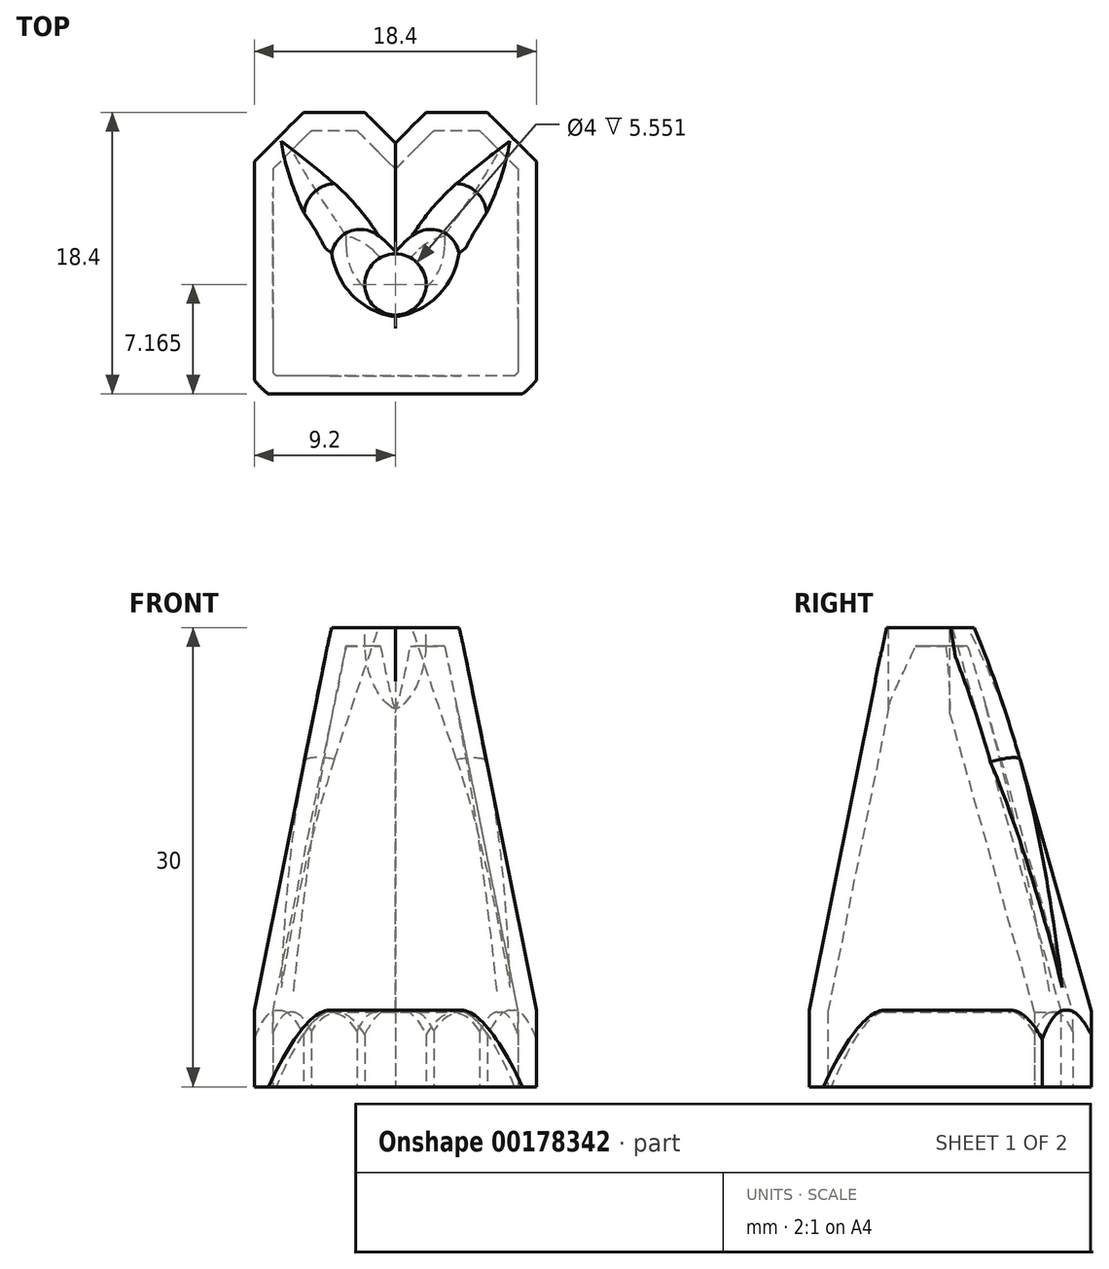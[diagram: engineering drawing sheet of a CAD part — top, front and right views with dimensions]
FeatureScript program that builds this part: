
annotation { "Feature Type Name" : "Feature", "Feature Type Description" : "" }
export const myFeature = defineFeature(function(context is Context, id is Id, definition is map)
    precondition{}
    {
        {
            var Q0;
            Q0=qCreatedBy(makeId("Top.planeOp"),FACE);
            var sketch = newSketch(context, id + "F0", { "sketchPlane" : qUnion([Q0])});
            skLineSegment(sketch, "E0.bottom", {"start": v(5.5, 8) * mm, "end": v(2.5, 8) * mm});
            skLineSegment(sketch, "E0.top", {"start": v(8, -8) * mm, "end": v(-8, -8) * mm});
            skLineSegment(sketch, "E0.left", {"start": v(8, 5.5) * mm, "end": v(8, -8) * mm});
            skLineSegment(sketch, "E0.right", {"start": v(-8, 5.5) * mm, "end": v(-8, -8) * mm});
            skPoint(sketch, "E0.middle", {"position": v(0, 0) * mm});
            skLineSegment(sketch, "E1", {"start": v(-2.5, 8) * mm, "end": v(0, 5.5) * mm});
            skLineSegment(sketch, "E2", {"start": v(0, 5.5) * mm, "end": v(2.5, 8) * mm});
            skLineSegment(sketch, "E3", {"start": v(-8, 5.5) * mm, "end": v(-5.5, 8) * mm});
            skLineSegment(sketch, "E4", {"start": v(8, 5.5) * mm, "end": v(5.5, 8) * mm});
            skPoint(sketch, "E5.orphan", {"position": v(-8, 8) * mm});
            skLineSegment(sketch, "E6.trimOffspring", {"start": v(-2.5, 8) * mm, "end": v(-5.5, 8) * mm});
            skPoint(sketch, "E7.orphan", {"position": v(8, 8) * mm});
            skLineSegment(sketch, "E8.0", {"start": v(-2, 9.2) * mm, "end": v(-6, 9.2) * mm});
            skLineSegment(sketch, "E8.1", {"start": v(-9.2, 6) * mm, "end": v(-6, 9.2) * mm});
            skLineSegment(sketch, "E8.2", {"start": v(-2, 9.2) * mm, "end": v(0, 7.2) * mm});
            skLineSegment(sketch, "E8.3", {"start": v(-9.2, 6) * mm, "end": v(-9.2, -9.2) * mm});
            skLineSegment(sketch, "E8.4", {"start": v(9.2, -9.2) * mm, "end": v(-9.2, -9.2) * mm});
            skLineSegment(sketch, "E8.5", {"start": v(0, 7.2) * mm, "end": v(2, 9.2) * mm});
            skLineSegment(sketch, "E8.6", {"start": v(6, 9.2) * mm, "end": v(2, 9.2) * mm});
            skLineSegment(sketch, "E8.7", {"start": v(9.2, 6) * mm, "end": v(6, 9.2) * mm});
            skLineSegment(sketch, "E8.8", {"start": v(9.2, 6) * mm, "end": v(9.2, -9.2) * mm});
            skSolve(sketch);
        }
        {
            var Q0;
            Q0=makeQuery(id+"F0.imprint","IMPRINT",FACE,{"disambiguationData":[TD([[makeQuery(id+"F0.imprint","IMPRINT",EDGE,{"derivedFrom":sQuery(id+"F0.wireOp",EDGE,"E0.bottom")}),-1.0]])]});
            var Q1;
            Q1=makeQuery(id+"F0.imprint","IMPRINT",FACE,{"disambiguationData":[TD([[makeQuery(id+"F0.imprint","IMPRINT",EDGE,{"derivedFrom":sQuery(id+"F0.wireOp",EDGE,"E0.bottom")}),1.0]])]});
            extrude(context, id + "F1", {"entities" : qUnion([Q0, Q1]), "depth" : 30 * mm});
        }
        {
            var Q0;
            Q0=makeQuery(id+"F1.opExtrude","CAP_EDGE",EDGE,{"disambiguationData":[OSD([sQuery(id+"F0.wireOp",EDGE,"E8.3")])],"isStart":false});
            var Q1;
            Q1=makeQuery(id+"F1.opExtrude","CAP_FACE",FACE,{"disambiguationData":[OSD([sQuery(id+"F0.wireOp",EDGE,"E8.0"),sQuery(id+"F0.wireOp",EDGE,"E8.1"),sQuery(id+"F0.wireOp",EDGE,"E8.2"),sQuery(id+"F0.wireOp",EDGE,"E8.3"),sQuery(id+"F0.wireOp",EDGE,"E8.4"),sQuery(id+"F0.wireOp",EDGE,"E8.5"),sQuery(id+"F0.wireOp",EDGE,"E8.6"),sQuery(id+"F0.wireOp",EDGE,"E8.7"),sQuery(id+"F0.wireOp",EDGE,"E8.8")])],"isStart":false});
            chamfer(context, id + "F2", {"entities" : qUnion([Q0, Q1]), "chamferType" : ChamferType.TWO_OFFSETS, "width1" : 5 * mm, "oppositeDirection" : false, "width2" : 25 * mm, "tangentPropagation" : true});
        }
        {
            var Q0;
            Q0=makeQuery(id+"F2.opChamfer","BLEND_EDGE",EDGE,{"blendedFrom":[makeQuery(id+"F1.opExtrude","CAP_EDGE",EDGE,{"disambiguationData":[OSD([sQuery(id+"F0.wireOp",EDGE,"E8.1")])],"isStart":false}),makeQuery(id+"F1.opExtrude","CAP_EDGE",EDGE,{"disambiguationData":[OSD([sQuery(id+"F0.wireOp",EDGE,"E8.2")])],"isStart":false})],"blendedInto":[]});
            var Q1;
            Q1=makeQuery(id+"F2.opChamfer","BLEND_EDGE",EDGE,{"blendedFrom":[makeQuery(id+"F1.opExtrude","CAP_EDGE",EDGE,{"disambiguationData":[OSD([sQuery(id+"F0.wireOp",EDGE,"E8.5")])],"isStart":false}),makeQuery(id+"F1.opExtrude","CAP_EDGE",EDGE,{"disambiguationData":[OSD([sQuery(id+"F0.wireOp",EDGE,"E8.7")])],"isStart":false})],"blendedInto":[]});
            var Q2;
            Q2=makeQuery(id+"F2.opChamfer","BLEND_EDGE",EDGE,{"blendedFrom":[makeQuery(id+"F1.opExtrude","CAP_EDGE",EDGE,{"disambiguationData":[OSD([sQuery(id+"F0.wireOp",EDGE,"E8.1")])],"isStart":false}),makeQuery(id+"F1.opExtrude","CAP_EDGE",EDGE,{"disambiguationData":[OSD([sQuery(id+"F0.wireOp",EDGE,"E8.3")])],"isStart":false})],"blendedInto":[]});
            var Q3;
            Q3=makeQuery(id+"F2.opChamfer","BLEND_EDGE",EDGE,{"blendedFrom":[makeQuery(id+"F1.opExtrude","CAP_EDGE",EDGE,{"disambiguationData":[OSD([sQuery(id+"F0.wireOp",EDGE,"E8.7")])],"isStart":false}),makeQuery(id+"F1.opExtrude","CAP_EDGE",EDGE,{"disambiguationData":[OSD([sQuery(id+"F0.wireOp",EDGE,"E8.8")])],"isStart":false})],"blendedInto":[]});
            var Q4;
            Q4=makeQuery(id+"F2.opChamfer","BLEND_EDGE",EDGE,{"blendedFrom":[makeQuery(id+"F1.opExtrude","CAP_EDGE",EDGE,{"disambiguationData":[OSD([sQuery(id+"F0.wireOp",EDGE,"E8.3")])],"isStart":false}),makeQuery(id+"F1.opExtrude","CAP_EDGE",EDGE,{"disambiguationData":[OSD([sQuery(id+"F0.wireOp",EDGE,"E8.4")])],"isStart":false})],"blendedInto":[]});
            var Q5;
            Q5=makeQuery(id+"F2.opChamfer","BLEND_EDGE",EDGE,{"blendedFrom":[makeQuery(id+"F1.opExtrude","CAP_EDGE",EDGE,{"disambiguationData":[OSD([sQuery(id+"F0.wireOp",EDGE,"E8.4")])],"isStart":false}),makeQuery(id+"F1.opExtrude","CAP_EDGE",EDGE,{"disambiguationData":[OSD([sQuery(id+"F0.wireOp",EDGE,"E8.8")])],"isStart":false})],"blendedInto":[]});
            fillet(context, id + "F3", {"entities" : qUnion([Q0, Q1, Q2, Q3, Q4, Q5]), "radius" : 5 * mm, "tangentPropagation" : true, "allowEdgeOverflow" : false});
        }
        {
            var Q0;
            Q0=makeQuery(id+"F1.opExtrude","CAP_FACE",FACE,{"disambiguationData":[OSD([sQuery(id+"F0.wireOp",EDGE,"E8.0"),sQuery(id+"F0.wireOp",EDGE,"E8.1"),sQuery(id+"F0.wireOp",EDGE,"E8.2"),sQuery(id+"F0.wireOp",EDGE,"E8.3"),sQuery(id+"F0.wireOp",EDGE,"E8.4"),sQuery(id+"F0.wireOp",EDGE,"E8.5"),sQuery(id+"F0.wireOp",EDGE,"E8.6"),sQuery(id+"F0.wireOp",EDGE,"E8.7"),sQuery(id+"F0.wireOp",EDGE,"E8.8")])],"isStart":true});
            shell(context, id + "F4", {"entities" : qUnion([Q0]), "thickness" : 1.2 * mm});
        }
        {
            var Q0;
            Q0=makeQuery(id+"F1.opExtrude","CAP_FACE",FACE,{"disambiguationData":[OSD([sQuery(id+"F0.wireOp",EDGE,"E8.0"),sQuery(id+"F0.wireOp",EDGE,"E8.1"),sQuery(id+"F0.wireOp",EDGE,"E8.2"),sQuery(id+"F0.wireOp",EDGE,"E8.3"),sQuery(id+"F0.wireOp",EDGE,"E8.4"),sQuery(id+"F0.wireOp",EDGE,"E8.5"),sQuery(id+"F0.wireOp",EDGE,"E8.6"),sQuery(id+"F0.wireOp",EDGE,"E8.7"),sQuery(id+"F0.wireOp",EDGE,"E8.8")])],"isStart":false});
            var sketch = newSketch(context, id + "F5", { "sketchPlane" : qUnion([Q0])});
            skCircle(sketch, "E9", {"center": v(0, -2.03) * mm, "radius": 2 * mm});
            skSolve(sketch);
        }
        {
            var Q0;
            Q0 = qSketchRegion(id + "F5", true);
            extrude(context, id + "F6", {"entities" : qUnion([Q0]), "operationType" : NewBodyOperationType.REMOVE, "endBound" : BoundingType.UP_TO_NEXT, "oppositeDirection" : true, "depth" : 25 * mm});
        }
        {
            var Q0;
            {var subQ0=makeQuery(id+"F1.opExtrude","CAP_EDGE",EDGE,{"disambiguationData":[OSD([sQuery(id+"F0.wireOp",EDGE,"E8.1")])],"isStart":false});Q0=makeQuery(id+"F3.opFillet","BLEND_EDGE",EDGE,{"blendedFrom":[makeQuery(id+"F2.opChamfer","BLEND_EDGE",EDGE,{"blendedFrom":[subQ0,makeQuery(id+"F1.opExtrude","CAP_EDGE",EDGE,{"disambiguationData":[OSD([sQuery(id+"F0.wireOp",EDGE,"E8.2")])],"isStart":false})],"blendedInto":[]}),makeQuery(id+"F2.opChamfer","BLEND_EDGE",EDGE,{"blendedFrom":[subQ0,makeQuery(id+"F1.opExtrude","CAP_EDGE",EDGE,{"disambiguationData":[OSD([sQuery(id+"F0.wireOp",EDGE,"E8.3")])],"isStart":false})],"blendedInto":[]})],"blendedInto":[]});}
            var Q1;
            {var subQ0=makeQuery(id+"F1.opExtrude","CAP_EDGE",EDGE,{"disambiguationData":[OSD([sQuery(id+"F0.wireOp",EDGE,"E8.7")])],"isStart":false});Q1=makeQuery(id+"F3.opFillet","BLEND_EDGE",EDGE,{"blendedFrom":[makeQuery(id+"F2.opChamfer","BLEND_EDGE",EDGE,{"blendedFrom":[makeQuery(id+"F1.opExtrude","CAP_EDGE",EDGE,{"disambiguationData":[OSD([sQuery(id+"F0.wireOp",EDGE,"E8.5")])],"isStart":false}),subQ0],"blendedInto":[]}),makeQuery(id+"F2.opChamfer","BLEND_EDGE",EDGE,{"blendedFrom":[subQ0,makeQuery(id+"F1.opExtrude","CAP_EDGE",EDGE,{"disambiguationData":[OSD([sQuery(id+"F0.wireOp",EDGE,"E8.8")])],"isStart":false})],"blendedInto":[]})],"blendedInto":[]});}
            fillet(context, id + "F7", {"entities" : qUnion([Q0, Q1]), "radius" : 2 * mm, "tangentPropagation" : true, "allowEdgeOverflow" : false});
        }
    });
